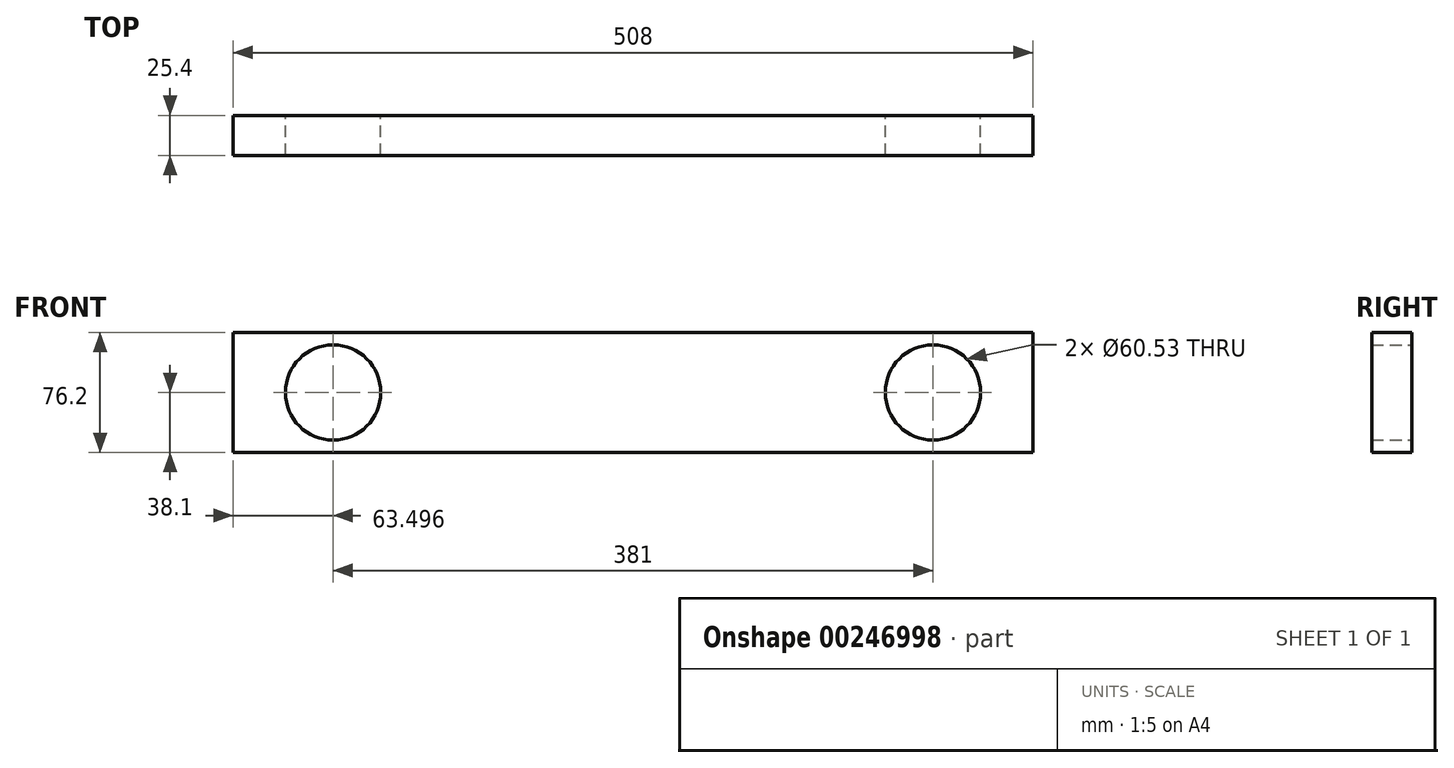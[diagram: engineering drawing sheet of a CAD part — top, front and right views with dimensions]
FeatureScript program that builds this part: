
annotation { "Feature Type Name" : "Feature", "Feature Type Description" : "" }
export const myFeature = defineFeature(function(context is Context, id is Id, definition is map)
    precondition{}
    {
        {
            var Q0;
            Q0=qCreatedBy(makeId("Front.planeOp"),FACE);
            var sketch = newSketch(context, id + "F0", { "sketchPlane" : qUnion([Q0])});
            skLineSegment(sketch, "E0", {"start": v(156.97, 38.1) * mm, "end": v(156.97, -38.1) * mm});
            skLineSegment(sketch, "E1", {"start": v(156.97, -38.1) * mm, "end": v(664.97, -38.1) * mm});
            skLineSegment(sketch, "E2", {"start": v(664.97, -38.1) * mm, "end": v(664.97, 38.1) * mm});
            skLineSegment(sketch, "E3", {"start": v(664.97, 38.1) * mm, "end": v(156.97, 38.1) * mm});
            skCircle(sketch, "E4", {"center": v(601.47, 0) * mm, "radius": 30.26 * mm});
            skCircle(sketch, "E5", {"center": v(220.47, 0) * mm, "radius": 30.26 * mm});
            skSolve(sketch);
        }
        {
            var Q0;
            Q0=makeQuery(id+"F0.imprint","IMPRINT",FACE,{"disambiguationData":[TD([[makeQuery(id+"F0.imprint","IMPRINT",EDGE,{"derivedFrom":sQuery(id+"F0.wireOp",EDGE,"E0")}),1.0]])]});
            extrude(context, id + "F1", {"entities" : qUnion([Q0]), "endBound" : BoundingType.SYMMETRIC, "depth" : 25.4 * mm});
        }
    });
